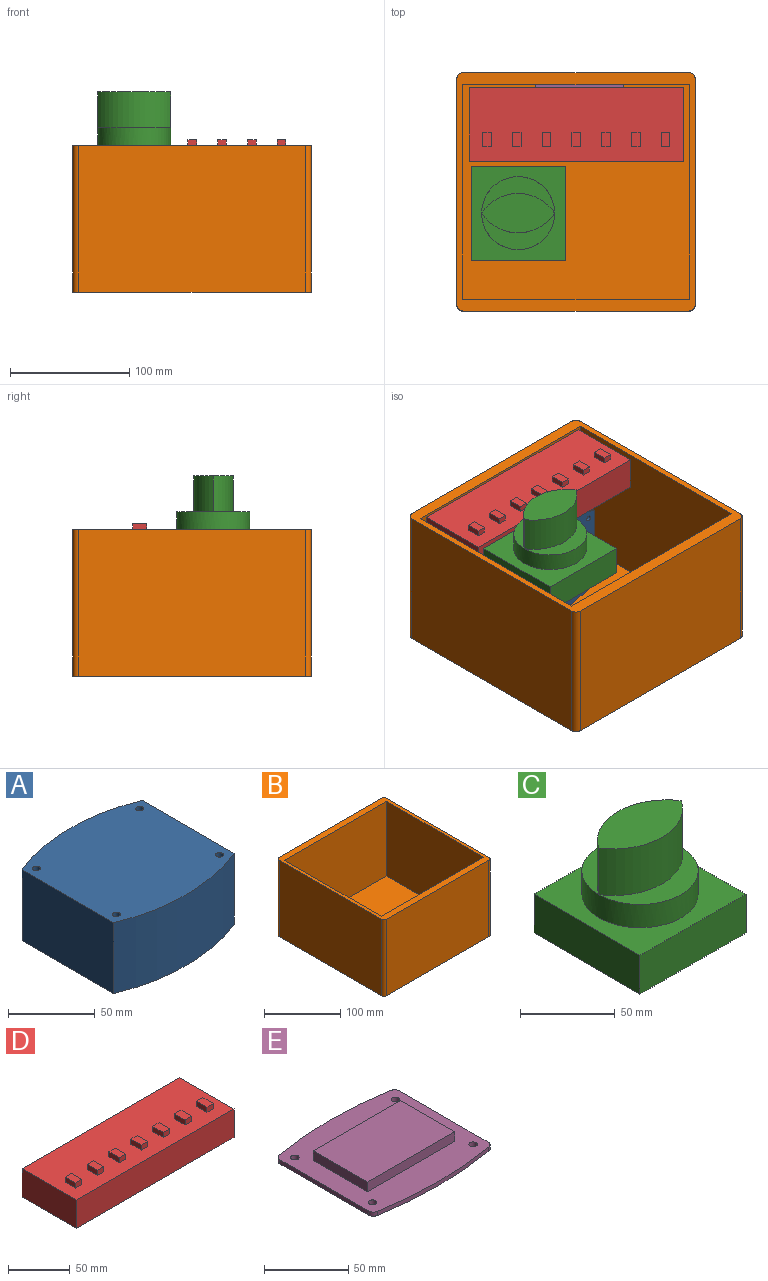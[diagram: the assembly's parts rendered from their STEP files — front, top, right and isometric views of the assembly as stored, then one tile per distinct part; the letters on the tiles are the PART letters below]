
ASSEMBLY  parts=5 mates=4
PART A: 10 faces, bbox 98.1x94.3x50 mm
  f0: plane 74.6x50mm, normal (-1,0,0), area 3730.1mm2, adj f1,f3,f4,f5
  f1: cylinder r=127.15mm len=98.14mm, axis (0,0,-1), area 5037.8mm2, adj f0,f2,f4,f5
  f2: plane 74.6x50mm, normal (1,0,0), area 3730.1mm2, adj f1,f3,f4,f5
  f3: cylinder r=127.15mm len=98.14mm, axis (0,0,-1), area 5037.8mm2, adj f0,f2,f4,f5
  f4: plane 98.14x94.3mm, normal (0,0,1), area 8557.1mm2, adj f0,f1,f2,f3,f6,f7,f8,f9
  f5: plane 98.14x94.3mm, normal (0,0,-1), area 8557.1mm2, adj f0,f1,f2,f3,f6,f7,f8,f9
  f6: cylinder r=2.25mm len=50mm, axis (0,0,1), area 706.9mm2, adj f4,f5
  f7: cylinder r=2.25mm len=50mm, axis (0,0,1), area 706.9mm2, adj f4,f5
  f8: cylinder r=2.25mm len=50mm, axis (0,0,1), area 706.9mm2, adj f4,f5
  f9: cylinder r=2.25mm len=50mm, axis (0,0,1), area 706.9mm2, adj f4,f5
PART B: 15 faces, bbox 200x200x123 mm
  f0: plane 190x123mm, normal (0,-1,0), area 23370mm2, adj f4,f9,f11,f14
  f1: plane 190x123mm, normal (1,0,0), area 23370mm2, adj f4,f9,f11,f12
  f2: plane 190x123mm, normal (0,1,0), area 23370mm2, adj f4,f9,f12,f13
  f3: plane 190x123mm, normal (-1,0,0), area 23370mm2, adj f4,f9,f13,f14
  f4: plane 200x200mm, normal (0,0,-1), area 39978.5mm2, adj f0,f1,f2,f3,f11,f12,f13,f14
  f5: plane 180x120mm, normal (-1,0,0), area 21600mm2, adj f6,f8,f9,f10
  f6: plane 190x120mm, normal (0,1,0), area 22800mm2, adj f5,f7,f9,f10
  f7: plane 180x120mm, normal (1,0,0), area 21600mm2, adj f6,f8,f9,f10
  f8: plane 190x120mm, normal (0,-1,0), area 22800mm2, adj f5,f7,f9,f10
  f9: plane 200x200mm, normal (0,0,1), area 5778.5mm2, adj f0,f1,f2,f3,f5,f6,f7,f8
  f10: plane 190x180mm, normal (0,0,1), area 34200mm2, adj f5,f6,f7,f8
  f11: cylinder r=5mm len=123mm, axis (0,0,-1), area 966mm2, adj f0,f1,f4,f9
  f12: cylinder r=5mm len=123mm, axis (0,0,1), area 966mm2, adj f1,f2,f4,f9
  f13: cylinder r=5mm len=123mm, axis (0,0,-1), area 966mm2, adj f2,f3,f4,f9
  f14: cylinder r=5mm len=123mm, axis (0,0,1), area 966mm2, adj f0,f3,f4,f9
PART C: 12 faces, bbox 79x79x70 mm
  f0: plane 61.28x30.64mm, normal (0,0,1), area 758.7mm2, adj f7,f9
  f1: plane 79x25mm, normal (0,-1,0), area 1975mm2, adj f2,f4,f5,f6
  f2: plane 79x25mm, normal (1,0,0), area 1975mm2, adj f1,f3,f5,f6
  f3: plane 79x25mm, normal (0,1,0), area 1975mm2, adj f2,f4,f5,f6
  f4: plane 79x25mm, normal (-1,0,0), area 1975mm2, adj f1,f3,f5,f6
  f5: plane 79x79mm, normal (0,0,1), area 3291.6mm2, adj f1,f2,f3,f4,f7
  f6: plane 79x79mm, normal (0,0,-1), area 6241mm2, adj f1,f2,f3,f4
  f7: cylinder r=30.64mm len=61.28mm, axis (0,0,-1), area 2887.7mm2, adj f0,f5,f8
  f8: plane 61.28x30.64mm, normal (0,0,1), area 758.7mm2, adj f7,f10
  f9: cylinder r=36.59mm len=61.28mm, axis (0,0,-1), area 2178.9mm2, adj f0,f10,f11
  f10: cylinder r=36.59mm len=61.28mm, axis (0,0,-1), area 2178.9mm2, adj f8,f9,f11
  f11: plane 61.28x33.18mm, normal (0,0,1), area 1431.9mm2, adj f9,f10
PART D: 41 faces, bbox 180x62x33 mm
  f0: plane 180x62mm, normal (0,0,1), area 10553.6mm2, adj f1,f2,f3,f4,f6,f7,f8,f9
  f1: plane 180x28mm, normal (0,-1,0), area 5040mm2, adj f0,f2,f4,f5
  f2: plane 62x28mm, normal (1,0,0), area 1736mm2, adj f0,f1,f3,f5
  f3: plane 180x28mm, normal (0,1,0), area 5040mm2, adj f0,f2,f4,f5
  f4: plane 62x28mm, normal (-1,0,0), area 1736mm2, adj f0,f1,f3,f5
  f5: plane 180x62mm, normal (0,0,-1), area 11160mm2, adj f1,f2,f3,f4
  f6: plane 7.26x5mm, normal (0,-1,0), area 36.3mm2, adj f0,f7,f9,f10
  f7: plane 11.94x5mm, normal (1,0,0), area 59.7mm2, adj f0,f6,f8,f10
  f8: plane 7.26x5mm, normal (0,1,0), area 36.3mm2, adj f0,f7,f9,f10
  f9: plane 11.94x5mm, normal (-1,0,0), area 59.7mm2, adj f0,f6,f8,f10
  f10: plane 11.94x7.26mm, normal (0,0,1), area 86.6mm2, adj f6,f7,f8,f9
  f11: plane 11.94x5mm, normal (-1,0,0), area 59.7mm2, adj f0,f12,f14,f15
  f12: plane 7.26x5mm, normal (0,-1,0), area 36.3mm2, adj f0,f11,f13,f15
  f13: plane 11.94x5mm, normal (1,0,0), area 59.7mm2, adj f0,f12,f14,f15
  f14: plane 7.26x5mm, normal (0,1,0), area 36.3mm2, adj f0,f11,f13,f15
  f15: plane 11.94x7.26mm, normal (0,0,1), area 86.6mm2, adj f11,f12,f13,f14
  f16: plane 11.94x5mm, normal (-1,0,0), area 59.7mm2, adj f0,f17,f19,f20
  f17: plane 7.26x5mm, normal (0,-1,0), area 36.3mm2, adj f0,f16,f18,f20
  f18: plane 11.94x5mm, normal (1,0,0), area 59.7mm2, adj f0,f17,f19,f20
  f19: plane 7.26x5mm, normal (0,1,0), area 36.3mm2, adj f0,f16,f18,f20
  f20: plane 11.94x7.26mm, normal (0,0,1), area 86.6mm2, adj f16,f17,f18,f19
  f21: plane 11.94x5mm, normal (-1,0,0), area 59.7mm2, adj f0,f22,f24,f25
  f22: plane 7.26x5mm, normal (0,-1,0), area 36.3mm2, adj f0,f21,f23,f25
  f23: plane 11.94x5mm, normal (1,0,0), area 59.7mm2, adj f0,f22,f24,f25
  f24: plane 7.26x5mm, normal (0,1,0), area 36.3mm2, adj f0,f21,f23,f25
  f25: plane 11.94x7.26mm, normal (0,0,1), area 86.6mm2, adj f21,f22,f23,f24
  f26: plane 7.26x5mm, normal (0,-1,0), area 36.3mm2, adj f0,f27,f29,f30
  f27: plane 11.94x5mm, normal (1,0,0), area 59.7mm2, adj f0,f26,f28,f30
  f28: plane 7.26x5mm, normal (0,1,0), area 36.3mm2, adj f0,f27,f29,f30
  f29: plane 11.94x5mm, normal (-1,0,0), area 59.7mm2, adj f0,f26,f28,f30
  f30: plane 11.94x7.26mm, normal (0,0,1), area 86.6mm2, adj f26,f27,f28,f29
  f31: plane 7.26x5mm, normal (0,-1,0), area 36.3mm2, adj f0,f32,f34,f35
  f32: plane 11.94x5mm, normal (1,0,0), area 59.7mm2, adj f0,f31,f33,f35
  f33: plane 7.26x5mm, normal (0,1,0), area 36.3mm2, adj f0,f32,f34,f35
  f34: plane 11.94x5mm, normal (-1,0,0), area 59.7mm2, adj f0,f31,f33,f35
  f35: plane 11.94x7.26mm, normal (0,0,1), area 86.6mm2, adj f31,f32,f33,f34
  f36: plane 7.26x5mm, normal (0,-1,0), area 36.3mm2, adj f0,f37,f39,f40
  f37: plane 11.94x5mm, normal (1,0,0), area 59.7mm2, adj f0,f36,f38,f40
  f38: plane 7.26x5mm, normal (0,1,0), area 36.3mm2, adj f0,f37,f39,f40
  f39: plane 11.94x5mm, normal (-1,0,0), area 59.7mm2, adj f0,f36,f38,f40
  f40: plane 11.94x7.26mm, normal (0,0,1), area 86.6mm2, adj f36,f37,f38,f39
PART E: 19 faces, bbox 100x90x10 mm
  f0: plane 100x90mm, normal (0,0,1), area 5291.5mm2, adj f1,f2,f3,f4,f5,f6,f7,f8
  f1: cylinder r=278.51mm len=93.34mm, axis (0,0,-1), area 281.3mm2, adj f0,f9,f10,f11
  f2: plane 74.24x3mm, normal (1,0,0), area 222.7mm2, adj f0,f9,f10,f12
  f3: cylinder r=278.51mm len=93.34mm, axis (0,0,-1), area 281.3mm2, adj f0,f9,f12,f13
  f4: cylinder r=2.5mm len=5mm, axis (0,0,-1), area 47.1mm2, adj f0,f9
  f5: cylinder r=2.5mm len=5mm, axis (0,0,-1), area 47.1mm2, adj f0,f9
  f6: cylinder r=2.5mm len=5mm, axis (0,0,-1), area 47.1mm2, adj f0,f9
  f7: plane 74.24x3mm, normal (-1,0,0), area 222.7mm2, adj f0,f9,f11,f13
  f8: cylinder r=2.5mm len=5mm, axis (0,0,-1), area 47.1mm2, adj f0,f9
  f9: plane 100x90mm, normal (0,0,-1), area 8611.7mm2, adj f1,f2,f3,f4,f5,f6,f7,f8
  f10: cylinder r=4mm len=3.94mm, axis (0,0,-1), area 16.8mm2, adj f0,f1,f2,f9
  f11: cylinder r=4mm len=3.94mm, axis (0,0,-1), area 16.8mm2, adj f0,f1,f7,f9
  f12: cylinder r=4mm len=3.94mm, axis (0,0,-1), area 16.8mm2, adj f0,f2,f3,f9
  f13: cylinder r=4mm len=3.94mm, axis (0,0,-1), area 16.8mm2, adj f0,f3,f7,f9
  f14: plane 73.12x7mm, normal (0,-1,0), area 511.8mm2, adj f0,f15,f17,f18
  f15: plane 45.41x7mm, normal (1,0,0), area 317.9mm2, adj f0,f14,f16,f18
  f16: plane 73.12x7mm, normal (0,1,0), area 511.8mm2, adj f0,f15,f17,f18
  f17: plane 45.41x7mm, normal (-1,0,0), area 317.9mm2, adj f0,f14,f16,f18
  f18: plane 73.12x45.41mm, normal (0,0,1), area 3320.2mm2, adj f14,f15,f16,f17
PLACE A rot(axis=(1,0,0),90deg) t=(-0.06,80.15,-9.9)mm
PLACE B t=(-3.04,0.15,-57.61)mm fixed
PLACE C t=(-51.58,-17.75,37.39)mm
PLACE D t=(-2.81,56.81,34.39)mm
PLACE E rot(axis=(0,-0.71,-0.71),180deg) t=(-0.06,80.15,-9.9)mm
MATE fastened E.f5 <-> A.f9  axis (0,-1,0) through (42.01,80.15,22.65)mm
MATE planar B.f8 <-> E.f18  axis (0,-1,0) through (-3.04,90.15,-57.61)mm
MATE planar B.f9 <-> D.f0  axis (0,0,1) through (-3.04,0.15,62.39)mm
MATE planar C.f5 <-> B.f9  axis (0,0,1) through (-12.08,-57.25,62.39)mm
